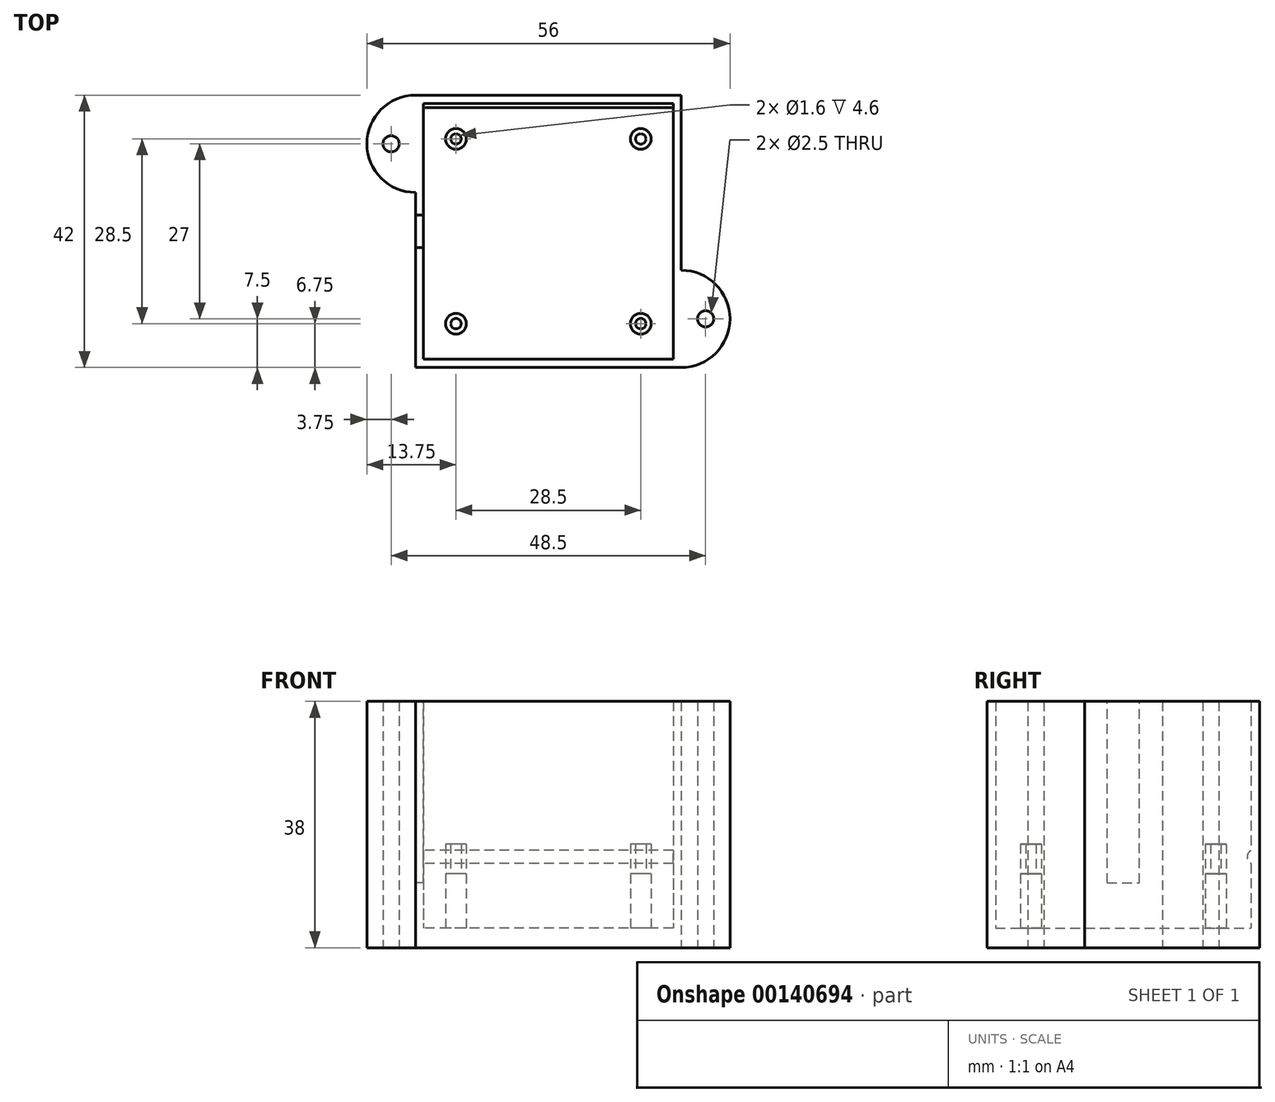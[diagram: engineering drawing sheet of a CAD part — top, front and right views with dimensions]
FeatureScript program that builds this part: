
annotation { "Feature Type Name" : "Feature", "Feature Type Description" : "" }
export const myFeature = defineFeature(function(context is Context, id is Id, definition is map)
    precondition{}
    {
        {
            var Q0;
            Q0=qCreatedBy(makeId("Top.planeOp"),FACE);
            var sketch = newSketch(context, id + "F0", { "sketchPlane" : qUnion([Q0])});
            skLineSegment(sketch, "E0.bottom", {"start": v(19.25, -19.7) * mm, "end": v(-19.25, -19.7) * mm});
            skLineSegment(sketch, "E0.top", {"start": v(19.25, 19.7) * mm, "end": v(-19.25, 19.7) * mm});
            skLineSegment(sketch, "E0.left", {"start": v(19.25, -19.7) * mm, "end": v(19.25, 19.7) * mm});
            skLineSegment(sketch, "E0.right", {"start": v(-19.25, -19.7) * mm, "end": v(-19.25, 19.7) * mm});
            skPoint(sketch, "E0.middle", {"position": v(0, 0) * mm});
            skLineSegment(sketch, "E1.bottom", {"start": v(-20.5, 21) * mm, "end": v(20.5, 21) * mm});
            skLineSegment(sketch, "E1.top", {"start": v(-20.5, -21) * mm, "end": v(20.5, -21) * mm});
            skLineSegment(sketch, "E1.left", {"start": v(-20.5, 21) * mm, "end": v(-20.5, -21) * mm});
            skLineSegment(sketch, "E1.right", {"start": v(20.5, 21) * mm, "end": v(20.5, -21) * mm});
            skLineSegment(sketch, "E2", {"start": v(-19.25, -19.7) * mm, "end": v(-14.25, -19.7) * mm, "construction": true});
            skLineSegment(sketch, "E3", {"start": v(-14.25, -19.7) * mm, "end": v(-14.25, -14.25) * mm, "construction": true});
            skCircle(sketch, "E4", {"center": v(-14.25, -14.25) * mm, "radius": 0.8 * mm});
            skCircle(sketch, "E5.MirrorC", {"center": v(14.25, -14.25) * mm, "radius": 0.8 * mm});
            skCircle(sketch, "E6.MirrorC", {"center": v(-14.25, 14.25) * mm, "radius": 0.8 * mm});
            skCircle(sketch, "E7.MirrorC", {"center": v(14.25, 14.25) * mm, "radius": 0.8 * mm});
            skArc(sketch, "E8", {"start": v(-20.5, 21) * mm, "mid": v(-28, 13.5) * mm, "end": v(-20.5, 6) * mm});
            skLineSegment(sketch, "E9", {"start": v(-20.5, 6) * mm, "end": v(-20.5, 21) * mm, "construction": true});
            skLineSegment(sketch, "E10", {"start": v(-20.5, 13.5) * mm, "end": v(-28, 13.5) * mm, "construction": true});
            skCircle(sketch, "E11", {"center": v(-24.25, 13.5) * mm, "radius": 1.25 * mm});
            skArc(sketch, "E12.MirrorCS", {"start": v(20.5, 21) * mm, "mid": v(28, 13.5) * mm, "end": v(20.5, 6) * mm});
            skCircle(sketch, "E13.MirrorC", {"center": v(24.25, 13.5) * mm, "radius": 1.25 * mm});
            skArc(sketch, "E14.MirrorCS", {"start": v(-20.5, -21) * mm, "mid": v(-28, -13.5) * mm, "end": v(-20.5, -6) * mm});
            skCircle(sketch, "E15.MirrorC", {"center": v(-24.25, -13.5) * mm, "radius": 1.25 * mm});
            skCircle(sketch, "E16.MirrorC", {"center": v(24.25, -13.5) * mm, "radius": 1.25 * mm});
            skArc(sketch, "E17.MirrorCS", {"start": v(20.5, -21) * mm, "mid": v(28, -13.5) * mm, "end": v(20.5, -6) * mm});
            skCircle(sketch, "E18", {"center": v(-14.25, -14.25) * mm, "radius": 1.6 * mm});
            skCircle(sketch, "E19.MirrorC", {"center": v(14.25, -14.25) * mm, "radius": 1.6 * mm});
            skCircle(sketch, "E20.MirrorC", {"center": v(-14.25, 14.25) * mm, "radius": 1.6 * mm});
            skCircle(sketch, "E21.MirrorC", {"center": v(14.25, 14.25) * mm, "radius": 1.6 * mm});
            skLineSegment(sketch, "E22", {"start": v(-14.25, 14.25) * mm, "end": v(14.25, 14.25) * mm, "construction": true});
            skLineSegment(sketch, "E23", {"start": v(14.25, 14.25) * mm, "end": v(14.25, -14.25) * mm, "construction": true});
            skSolve(sketch);
        }
        {
            var Q0;
            Q0=makeQuery(id+"F0.imprint","IMPRINT",FACE,{"disambiguationData":[TD([[makeQuery(id+"F0.imprint","IMPRINT",EDGE,{"derivedFrom":sQuery(id+"F0.wireOp",EDGE,"E0.bottom")}),-1.0]])]});
            extrude(context, id + "F1", {"entities" : qUnion([Q0]), "depth" : 3 * mm});
        }
        {
            var Q0;
            Q0=makeQuery(id+"F0.imprint","IMPRINT",FACE,{"disambiguationData":[TD([[makeQuery(id+"F0.imprint","IMPRINT",EDGE,{"derivedFrom":sQuery(id+"F0.wireOp",EDGE,"E6.MirrorC")}),1.0]])]});
            var Q1;
            Q1=makeQuery(id+"F0.imprint","IMPRINT",FACE,{"disambiguationData":[TD([[makeQuery(id+"F0.imprint","IMPRINT",EDGE,{"derivedFrom":sQuery(id+"F0.wireOp",EDGE,"E4")}),-1.0]])]});
            var Q2;
            Q2=makeQuery(id+"F0.imprint","IMPRINT",FACE,{"disambiguationData":[TD([[makeQuery(id+"F0.imprint","IMPRINT",EDGE,{"derivedFrom":sQuery(id+"F0.wireOp",EDGE,"E5.MirrorC")}),1.0]])]});
            var Q3;
            Q3=makeQuery(id+"F0.imprint","IMPRINT",FACE,{"disambiguationData":[TD([[makeQuery(id+"F0.imprint","IMPRINT",EDGE,{"derivedFrom":sQuery(id+"F0.wireOp",EDGE,"E7.MirrorC")}),-1.0]])]});
            extrude(context, id + "F2", {"entities" : qUnion([Q0, Q1, Q2, Q3]), "operationType" : NewBodyOperationType.ADD, "depth" : 11.4 * mm});
        }
        {
            var Q0;
            Q0=makeQuery(id+"F0.imprint","IMPRINT",FACE,{"disambiguationData":[TD([[makeQuery(id+"F0.imprint","IMPRINT",EDGE,{"derivedFrom":sQuery(id+"F0.wireOp",EDGE,"E6.MirrorC")}),-1.0]])]});
            var Q1;
            Q1=makeQuery(id+"F0.imprint","IMPRINT",FACE,{"disambiguationData":[TD([[makeQuery(id+"F0.imprint","IMPRINT",EDGE,{"derivedFrom":sQuery(id+"F0.wireOp",EDGE,"E4")}),1.0]])]});
            var Q2;
            Q2=makeQuery(id+"F0.imprint","IMPRINT",FACE,{"disambiguationData":[TD([[makeQuery(id+"F0.imprint","IMPRINT",EDGE,{"derivedFrom":sQuery(id+"F0.wireOp",EDGE,"E5.MirrorC")}),-1.0]])]});
            var Q3;
            Q3=makeQuery(id+"F0.imprint","IMPRINT",FACE,{"disambiguationData":[TD([[makeQuery(id+"F0.imprint","IMPRINT",EDGE,{"derivedFrom":sQuery(id+"F0.wireOp",EDGE,"E7.MirrorC")}),1.0]])]});
            extrude(context, id + "F3", {"entities" : qUnion([Q0, Q1, Q2, Q3]), "operationType" : NewBodyOperationType.ADD, "depth" : 16 * mm});
        }
        {
            var Q0;
            Q0=makeQuery(id+"F0.imprint","IMPRINT",FACE,{"disambiguationData":[TD([[makeQuery(id+"F0.imprint","IMPRINT",EDGE,{"derivedFrom":sQuery(id+"F0.wireOp",EDGE,"E0.bottom")}),1.0]])]});
            var Q1;
            {var subQ0=sQuery(id+"F0.wireOp",EDGE,"E14.MirrorCS");Q1=makeQuery(id+"F0.imprint","IMPRINT",FACE,{"disambiguationData":[TD([[makeQuery(id+"F0.imprint","IMPRINT",EDGE,{"derivedFrom":subQ0}),-1.0]])]});}
            var Q2;
            Q2=makeQuery(id+"F0.imprint","IMPRINT",FACE,{"disambiguationData":[TD([[makeQuery(id+"F0.imprint","IMPRINT",EDGE,{"derivedFrom":sQuery(id+"F0.wireOp",EDGE,"E16.MirrorC")}),-1.0]])]});
            var Q3;
            {var subQ0=sQuery(id+"F0.wireOp",EDGE,"E12.MirrorCS");Q3=makeQuery(id+"F0.imprint","IMPRINT",FACE,{"disambiguationData":[TD([[makeQuery(id+"F0.imprint","IMPRINT",EDGE,{"derivedFrom":subQ0}),-1.0]])]});}
            var Q4;
            {var subQ0=sQuery(id+"F0.wireOp",EDGE,"E8");Q4=makeQuery(id+"F0.imprint","IMPRINT",FACE,{"disambiguationData":[TD([[makeQuery(id+"F0.imprint","IMPRINT",EDGE,{"derivedFrom":subQ0}),1.0]])]});}
            extrude(context, id + "F4", {"entities" : qUnion([Q0, Q1, Q2, Q3, Q4]), "operationType" : NewBodyOperationType.ADD, "depth" : 38 * mm});
        }
        {
            var Q0;
            Q0=makeQuery(id+"F4.opExtrude","CAP_FACE",FACE,{"disambiguationData":[OSD([sQuery(id+"F0.wireOp",EDGE,"E0.bottom"),sQuery(id+"F0.wireOp",EDGE,"E0.top"),sQuery(id+"F0.wireOp",EDGE,"E0.left"),sQuery(id+"F0.wireOp",EDGE,"E0.right"),sQuery(id+"F0.wireOp",EDGE,"E1.bottom"),sQuery(id+"F0.wireOp",EDGE,"E1.top"),sQuery(id+"F0.wireOp",EDGE,"E1.left"),sQuery(id+"F0.wireOp",EDGE,"E1.right"),sQuery(id+"F0.wireOp",EDGE,"E8"),sQuery(id+"F0.wireOp",EDGE,"E11"),sQuery(id+"F0.wireOp",EDGE,"E12.MirrorCS"),sQuery(id+"F0.wireOp",EDGE,"E13.MirrorC"),sQuery(id+"F0.wireOp",EDGE,"E14.MirrorCS"),sQuery(id+"F0.wireOp",EDGE,"E15.MirrorC"),sQuery(id+"F0.wireOp",EDGE,"E16.MirrorC"),sQuery(id+"F0.wireOp",EDGE,"E17.MirrorCS")])],"isStart":false});
            var sketch = newSketch(context, id + "F5", { "sketchPlane" : qUnion([Q0])});
            skLineSegment(sketch, "E24", {"start": v(-19.25, 0) * mm, "end": v(-20.5, 0) * mm, "construction": true});
            skLineSegment(sketch, "E25.bottom", {"start": v(-19.25, -2.5) * mm, "end": v(-20.5, -2.5) * mm});
            skLineSegment(sketch, "E25.top", {"start": v(-19.25, 2.5) * mm, "end": v(-20.5, 2.5) * mm});
            skLineSegment(sketch, "E25.left", {"start": v(-19.25, -2.5) * mm, "end": v(-19.25, 2.5) * mm});
            skLineSegment(sketch, "E25.right", {"start": v(-20.5, -2.5) * mm, "end": v(-20.5, 2.5) * mm});
            skPoint(sketch, "E25.middle", {"position": v(-19.88, 0) * mm});
            skSolve(sketch);
        }
        {
            var Q0;
            Q0=makeQuery(id+"F5.imprint","IMPRINT",FACE,{"disambiguationData":[TD([[makeQuery(id+"F5.imprint","IMPRINT",EDGE,{"derivedFrom":sQuery(id+"F5.wireOp",EDGE,"E25.bottom")}),-1.0]])]});
            extrude(context, id + "F6", {"entities" : qUnion([Q0]), "operationType" : NewBodyOperationType.REMOVE, "oppositeDirection" : true, "depth" : 28 * mm});
        }
        {
            var Q0;
            Q0=makeQuery(id+"F4.opExtrude","CAP_FACE",FACE,{"disambiguationData":[OSD([sQuery(id+"F0.wireOp",EDGE,"E0.bottom"),sQuery(id+"F0.wireOp",EDGE,"E0.top"),sQuery(id+"F0.wireOp",EDGE,"E0.left"),sQuery(id+"F0.wireOp",EDGE,"E0.right"),sQuery(id+"F0.wireOp",EDGE,"E1.bottom"),sQuery(id+"F0.wireOp",EDGE,"E1.top"),sQuery(id+"F0.wireOp",EDGE,"E1.left"),sQuery(id+"F0.wireOp",EDGE,"E1.right"),sQuery(id+"F0.wireOp",EDGE,"E8"),sQuery(id+"F0.wireOp",EDGE,"E11"),sQuery(id+"F0.wireOp",EDGE,"E12.MirrorCS"),sQuery(id+"F0.wireOp",EDGE,"E13.MirrorC"),sQuery(id+"F0.wireOp",EDGE,"E14.MirrorCS"),sQuery(id+"F0.wireOp",EDGE,"E15.MirrorC"),sQuery(id+"F0.wireOp",EDGE,"E16.MirrorC"),sQuery(id+"F0.wireOp",EDGE,"E17.MirrorCS")])],"isStart":false});
            cPlane(context, id + "F7", {"entities" : qUnion([Q0]), "cplaneType" : CPlaneType.OFFSET, "offset" : 26.6 * mm, "oppositeDirection" : true, "width" : 150 * mm, "height" : 150 * mm});
        }
        {
            var Q0;
            Q0=makeQuery(id+"F4.opExtrude","SWEPT_FACE",FACE,{"disambiguationData":[OSD([sQuery(id+"F0.wireOp",EDGE,"E0.top")])]});
            var sketch = newSketch(context, id + "F8", { "sketchPlane" : qUnion([Q0])});
            skLineSegment(sketch, "E26", {"start": v(0, 11.4) * mm, "end": v(0, 13) * mm, "construction": true});
            skLineSegment(sketch, "E27", {"start": v(0, 13) * mm, "end": v(0, 15) * mm, "construction": true});
            skSolve(sketch);
        }
        {
            var Q0;
            Q0=qCreatedBy(makeId("Right.planeOp"),FACE);
            var sketch = newSketch(context, id + "F9", { "sketchPlane" : qUnion([Q0])});
            skArc(sketch, "E28", {"start": v(19.7, 15) * mm, "mid": v(19.11, 14) * mm, "end": v(19.7, 13) * mm});
            skLineSegment(sketch, "E29", {"start": v(19.7, 15) * mm, "end": v(19.7, 13) * mm});
            skArc(sketch, "E30.MirrorCS", {"start": v(-19.7, 15) * mm, "mid": v(-19.11, 14) * mm, "end": v(-19.7, 13) * mm});
            skLineSegment(sketch, "E31.MirrorCS", {"start": v(-19.7, 15) * mm, "end": v(-19.7, 13) * mm});
            skSolve(sketch);
        }
        {
            var Q0;
            Q0=makeQuery(id+"F9.imprint","IMPRINT",FACE,{"disambiguationData":[TD([[makeQuery(id+"F9.imprint","IMPRINT",EDGE,{"derivedFrom":sQuery(id+"F9.wireOp",EDGE,"E28")}),1.0]])]});
            var Q1;
            Q1=makeQuery(id+"F9.imprint","IMPRINT",FACE,{"disambiguationData":[TD([[makeQuery(id+"F9.imprint","IMPRINT",EDGE,{"derivedFrom":sQuery(id+"F9.wireOp",EDGE,"E30.MirrorCS")}),-1.0]])]});
            var Q2;
            Q2=makeQuery(id+"F4.opExtrude","SWEPT_FACE",FACE,{"disambiguationData":[OSD([sQuery(id+"F0.wireOp",EDGE,"E0.left")])]});
            var Q3;
            Q3=makeQuery(id+"F4.opExtrude","SWEPT_FACE",FACE,{"disambiguationData":[OSD([sQuery(id+"F0.wireOp",EDGE,"E0.right")])]});
            extrude(context, id + "F10", {"entities" : qUnion([Q0, Q1]), "operationType" : NewBodyOperationType.ADD, "endBound" : BoundingType.UP_TO_SURFACE, "endBoundEntityFace" : qUnion([Q2]), "depth" : 25 * mm, "hasSecondDirection" : true, "secondDirectionBound" : SecondDirectionBoundingType.UP_TO_SURFACE, "secondDirectionOppositeDirection" : true, "secondDirectionBoundEntityFace" : qUnion([Q3]), "secondDirectionDepth" : 25 * mm});
        }
    });
